# Revit family: IS_Connect_E0256_BIM_FR
name_source: partatom
category: Plumbing Fixtures
revit_build: Autodesk Revit 2017 (Build: 20160225_1515(x64)
units: mm (PartAtom-declared; Revit-internal decimal feet)

## family parameters
Always vertical = No
Cut with Voids When Loaded = No
OmniClass Number = 23.45.05.14.21
OmniClass Title = Bathtubs
Part Type = Normal
Room Calculation Point = No
Round Connector Dimension = Use Diameter
Shared = No
Work Plane-Based = No

## types (1)
- E025601 - CONNECT TAB  BAIN ECO EAU G 170 cm  BLC
    Accessoires = www.idealspec.fr
    Auteur = Ideal Standard
    BIMobject category = Bath & Spas
    BIMobject category code = sanitary-bath-spas
    BIMobject main category = Sanitary
    BIMobject main category code = sanitary
    BOSUseNativeGeometries = 1
    Bim-NomDuProjet = ISI_IdealStandard_Baths_CONNECT_E025601
    Brand url = www.idealspec.fr
    Caractéristiques = CONNECT F/PANEL 170 WHITE LH SPC/SVG
    CodeBarre = 5017830400790
    Conformité = NF
    ConseilsDInstallation = 0
    Cost = 0 $
    Couleur = Blanc
    CoûtDeRemplacement = 0
    Date of publishing = 2018_07_24
    DateDeCréation = 2018_07_24
    Description = CONNECT Tablier pour baignoire version gauche
    DiamètreÉvacuation = 0
    Dimensions = 1700 x 700 x 450 mm
    EAN code = https://5017830400790
    Edition number = 1
    Espace = Interne
    Finition = Blanc
    Forme = Complexe
    Hauteur = 450 mm
    IFC Classification = Sanitary Terminal
    IfcExportAs = BATH
    IfcExportType = IfcSanitaryTerminalType
    InformationsProduit = www.idealspec.fr
    Installation instructions = http://www.idealspec.fr
    Largeur = 700 mm
    Longueur = 1700 mm  [stored 5.57743 ft]
    Manufacturer name = Ideal Standard
    Marque = Ideal Standard
    Material main = Acrylic
    Matériel = Acrylic
    Model = E025601
    NBS Reference Code = 35-06-08
    NBS Reference Description = Baths
    Nominal height = 0
    Nominal width = 1700
    OmniClass Code = 23-31 15 00
    OmniClass Description = Bathtubs
    PoignéesDePréhension = No
    Product Guid = e56d2d47-b9d3-4806-a9ce-884c214213b2
    Product SKU = E0256
    Product certification = http://www.idealspec.fr
    Product data url = https://bimobject.com
    Product family = CONNECT
    Product group = Bath Tub
    Product name = CONNECT F/PANEL 170 WHITE LH SPC/SVG
    Product url = http://www.idealspec.fr
    Profondeur = 0 mm  [stored 0 ft]
    QR code = http://bimobject.com
    Raccordement = Plomberie
    Révision = 1
    Technical description = http://www.idealspec.fr
    TypeDeBaignoire = Domestic
    UNSPSC Code = 30181501
    URL = www.idealspec.fr
    Uniclass 1.4 Code = L7211
    Uniclass 1.4 Description = Baths
    Uniclass 2.0 Code = PR-35-06-08
    Uniclass 2.0 Description = Baths
    Uniclass 2015 Code = Pr_40_20_06_08
    Uniclass 2015 Name = Baths
    Uniclass2015Code = Pr_40_20_06_08
    Uniclass2015Title = Baths
    Uniclass2015Version = Products v1.1
    UnitéDeMesure = Millimètres
    UnitéDeTemps = An
    UnitéMonétaire = €
    UrlDuFabricant = www.idealspec.fr
    Version = 1
    Weight Net (Kg) = 3.4
    Youtube clip = http://www.idealspec.fr

note: [stored X ft] marks values corroborated as IEEE doubles in the binary element streams (Revit-internal decimal feet)

## geometry (parser evidence)
native form markers: Sweep x2
no freeform markers — native parametric forms only
